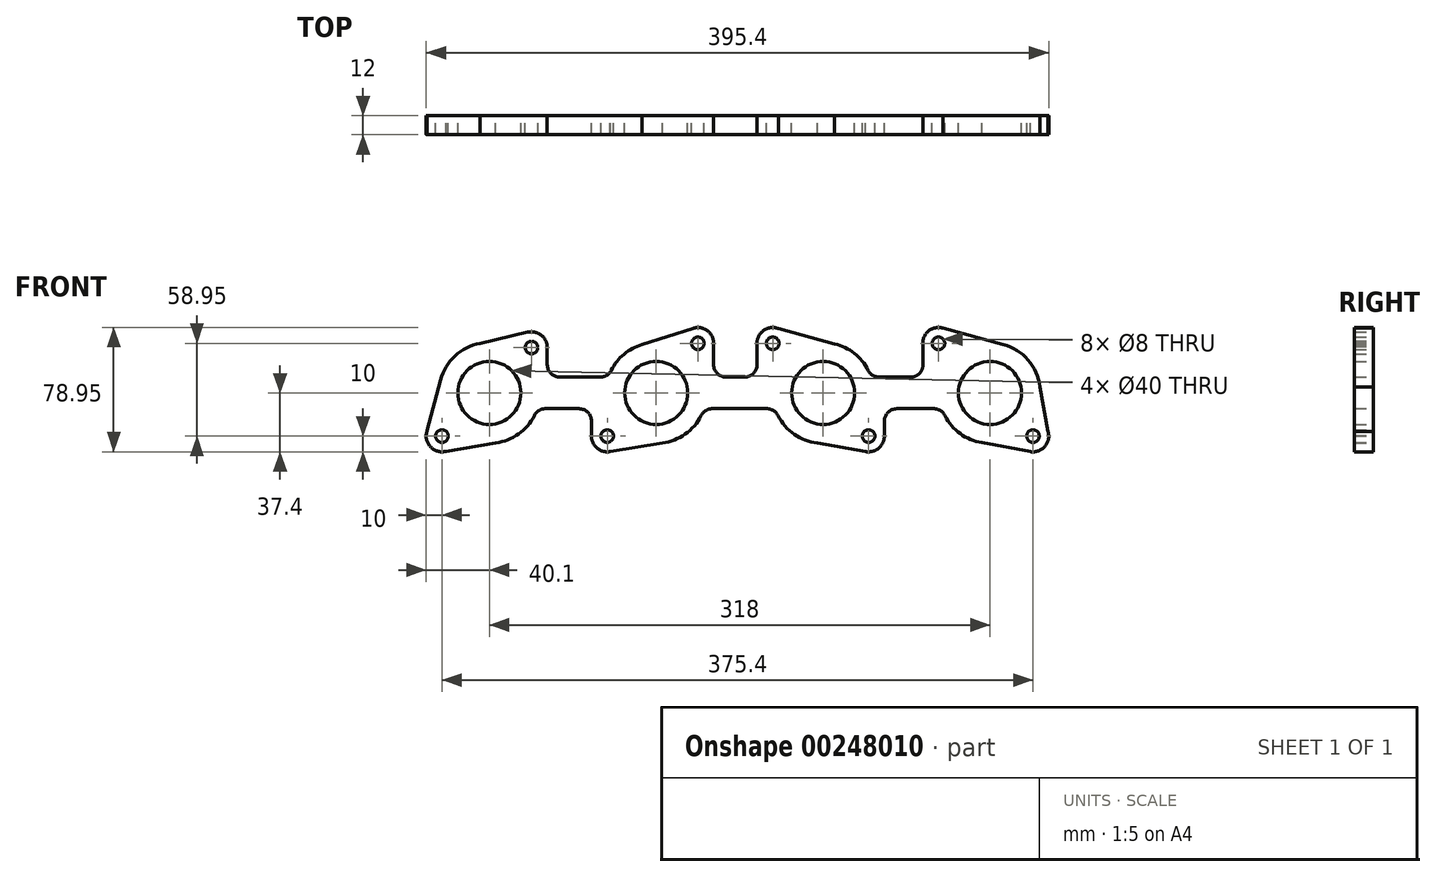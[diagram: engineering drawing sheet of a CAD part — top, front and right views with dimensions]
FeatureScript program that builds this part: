
annotation { "Feature Type Name" : "Feature", "Feature Type Description" : "" }
export const myFeature = defineFeature(function(context is Context, id is Id, definition is map)
    precondition{}
    {
        {
            var Q0;
            Q0=qCreatedBy(makeId("Front.planeOp"),FACE);
            var sketch = newSketch(context, id + "F0", { "sketchPlane" : qUnion([Q0])});
            skCircle(sketch, "E0", {"center": v(0, 0) * mm, "radius": 20 * mm});
            skCircle(sketch, "E1", {"center": v(106, 0) * mm, "radius": 20 * mm});
            skCircle(sketch, "E2", {"center": v(212, 0) * mm, "radius": 20 * mm});
            skCircle(sketch, "E3", {"center": v(26.8, 28.85) * mm, "radius": 4 * mm});
            skCircle(sketch, "E4", {"center": v(132.45, 31.55) * mm, "radius": 4 * mm});
            skCircle(sketch, "E5", {"center": v(180, 31.55) * mm, "radius": 4 * mm});
            skCircle(sketch, "E6", {"center": v(285.25, 31.55) * mm, "radius": 4 * mm});
            skCircle(sketch, "E7", {"center": v(-30.1, -27.4) * mm, "radius": 4 * mm});
            skCircle(sketch, "E8", {"center": v(74.9, -27.4) * mm, "radius": 4 * mm});
            skCircle(sketch, "E9", {"center": v(240.9, -27.4) * mm, "radius": 4 * mm});
            skCircle(sketch, "E10", {"center": v(345.3, -27.4) * mm, "radius": 4 * mm});
            skCircle(sketch, "E11", {"center": v(318, 0) * mm, "radius": 20 * mm});
            skArc(sketch, "E12", {"start": v(36.78, 28.3) * mm, "mid": v(33.2, 36.54) * mm, "end": v(24.43, 38.57) * mm});
            skArc(sketch, "E13", {"start": v(142.45, 31.49) * mm, "mid": v(138.37, 39.6) * mm, "end": v(129.4, 41.07) * mm});
            skArc(sketch, "E14", {"start": v(183.75, 40.82) * mm, "mid": v(174.24, 39.72) * mm, "end": v(170, 31.14) * mm});
            skArc(sketch, "E15", {"start": v(288.07, 41.14) * mm, "mid": v(279.2, 39.51) * mm, "end": v(275.25, 31.4) * mm});
            skArc(sketch, "E16", {"start": v(343.28, -37.2) * mm, "mid": v(352.72, -34.1) * mm, "end": v(354.84, -24.4) * mm});
            skArc(sketch, "E17", {"start": v(238.77, -37.17) * mm, "mid": v(247.26, -35.12) * mm, "end": v(250.9, -27.18) * mm});
            skArc(sketch, "E18", {"start": v(64.91, -26.93) * mm, "mid": v(68.36, -34.97) * mm, "end": v(76.8, -37.22) * mm});
            skArc(sketch, "E19", {"start": v(-39.46, -23.88) * mm, "mid": v(-37.48, -34.15) * mm, "end": v(-27.43, -37.04) * mm});
            skArc(sketch, "E20", {"start": v(240.58, 14.4) * mm, "mid": v(231.8, 25.14) * mm, "end": v(219.3, 31.16) * mm});
            skArc(sketch, "E21", {"start": v(289.42, -14.4) * mm, "mid": v(299.09, -25.81) * mm, "end": v(312.89, -31.59) * mm});
            skLineSegment(sketch, "E22", {"start": v(44.78, 10) * mm, "end": v(70.28, 10) * mm});
            skLineSegment(sketch, "E23", {"start": v(35.72, -10) * mm, "end": v(56.91, -10) * mm});
            skLineSegment(sketch, "E24.trimOffspring", {"start": v(150.45, 10) * mm, "end": v(162, 10) * mm});
            skLineSegment(sketch, "E25.trimOffspring", {"start": v(247.72, 10) * mm, "end": v(267.17, 10) * mm});
            skLineSegment(sketch, "E26.trimOffspring", {"start": v(258.9, -10) * mm, "end": v(282.28, -10) * mm});
            skArc(sketch, "E27.trimOffspring", {"start": v(183.42, -14.4) * mm, "mid": v(193.67, -26.23) * mm, "end": v(208.31, -31.79) * mm});
            skLineSegment(sketch, "E28.trimOffspring", {"start": v(141.72, -10) * mm, "end": v(176.28, -10) * mm});
            skArc(sketch, "E29.trimOffspring", {"start": v(109.88, -31.76) * mm, "mid": v(124.4, -26.18) * mm, "end": v(134.58, -14.4) * mm});
            skLineSegment(sketch, "E30", {"start": v(36.78, 29.4) * mm, "end": v(36.78, 18) * mm});
            skLineSegment(sketch, "E31", {"start": v(64.91, -26.93) * mm, "end": v(64.91, -18) * mm});
            skLineSegment(sketch, "E32", {"start": v(142.45, 31.61) * mm, "end": v(142.45, 18) * mm});
            skLineSegment(sketch, "E33", {"start": v(170, 31.96) * mm, "end": v(170, 18) * mm});
            skLineSegment(sketch, "E34", {"start": v(250.9, -27.18) * mm, "end": v(250.9, -18) * mm});
            skPoint(sketch, "E35.0.visualSharp", {"position": v(250.9, -10) * mm});
            skArc(sketch, "E35.0.filletArc", {"start": v(258.9, -10) * mm, "mid": v(253.24, -12.34) * mm, "end": v(250.9, -18) * mm});
            skPoint(sketch, "E36.0.newPointB", {"position": v(170, 10) * mm});
            skArc(sketch, "E36.0.filletArc", {"start": v(162, 10) * mm, "mid": v(167.67, 12.34) * mm, "end": v(170, 18) * mm});
            skPoint(sketch, "E37.0.newPointB", {"position": v(142.45, 10) * mm});
            skArc(sketch, "E37.0.filletArc", {"start": v(142.45, 18) * mm, "mid": v(144.8, 12.34) * mm, "end": v(150.45, 10) * mm});
            skArc(sketch, "E38.0.filletArc", {"start": v(64.91, -18) * mm, "mid": v(62.57, -12.34) * mm, "end": v(56.91, -10) * mm});
            skPoint(sketch, "E39.0.newPointA", {"position": v(36.78, 10) * mm});
            skArc(sketch, "E39.0.filletArc", {"start": v(36.78, 18) * mm, "mid": v(39.13, 12.34) * mm, "end": v(44.78, 10) * mm});
            skArc(sketch, "E40.trimOffspring", {"start": v(-5.87, 31.46) * mm, "mid": v(-21.76, 23.47) * mm, "end": v(-30.93, 8.22) * mm});
            skArc(sketch, "E41.trimOffspring", {"start": v(96.91, 30.68) * mm, "mid": v(85.48, 24.56) * mm, "end": v(77.42, 14.4) * mm});
            skLineSegment(sketch, "E42", {"start": v(219.3, 31.16) * mm, "end": v(183.75, 40.82) * mm});
            skLineSegment(sketch, "E43", {"start": v(238.77, -37.17) * mm, "end": v(208.31, -31.79) * mm});
            skLineSegment(sketch, "E44", {"start": v(96.91, 30.68) * mm, "end": v(129.4, 41.07) * mm});
            skLineSegment(sketch, "E45", {"start": v(109.88, -31.76) * mm, "end": v(76.8, -37.22) * mm});
            skPoint(sketch, "E45.endSnap0", {"position": v(76.8, -37.22) * mm});
            skLineSegment(sketch, "E46", {"start": v(76.8, -37.22) * mm, "end": v(76.8, -37.22) * mm});
            skPoint(sketch, "E47.0.visualSharp", {"position": v(75.6, 10) * mm});
            skArc(sketch, "E47.0.filletArc", {"start": v(70.28, 10) * mm, "mid": v(74.47, 11.19) * mm, "end": v(77.42, 14.4) * mm});
            skPoint(sketch, "E48.0.visualSharp", {"position": v(136.4, -10) * mm});
            skArc(sketch, "E48.0.filletArc", {"start": v(141.72, -10) * mm, "mid": v(137.53, -11.19) * mm, "end": v(134.58, -14.4) * mm});
            skPoint(sketch, "E49.0.visualSharp", {"position": v(181.6, -10) * mm});
            skArc(sketch, "E49.0.filletArc", {"start": v(183.42, -14.4) * mm, "mid": v(180.47, -11.19) * mm, "end": v(176.28, -10) * mm});
            skPoint(sketch, "E50.0.visualSharp", {"position": v(242.4, 10) * mm});
            skArc(sketch, "E50.0.filletArc", {"start": v(240.58, 14.4) * mm, "mid": v(243.53, 11.19) * mm, "end": v(247.72, 10) * mm});
            skPoint(sketch, "E51.0.visualSharp", {"position": v(287.6, -10) * mm});
            skArc(sketch, "E51.0.filletArc", {"start": v(289.42, -14.4) * mm, "mid": v(286.47, -11.19) * mm, "end": v(282.28, -10) * mm});
            skPoint(sketch, "E52.0.visualSharp", {"position": v(30.4, -10) * mm});
            skArc(sketch, "E52.0.filletArc", {"start": v(35.72, -10) * mm, "mid": v(31.53, -11.19) * mm, "end": v(28.58, -14.4) * mm});
            skLineSegment(sketch, "E53", {"start": v(24.43, 38.57) * mm, "end": v(-5.87, 31.46) * mm});
            skLineSegment(sketch, "E54", {"start": v(-39.46, -23.88) * mm, "end": v(-30.93, 8.22) * mm});
            skLineSegment(sketch, "E55", {"start": v(-27.43, -37.04) * mm, "end": v(4.09, -31.74) * mm});
            skArc(sketch, "E56.trimOffspring", {"start": v(4.09, -31.74) * mm, "mid": v(18.49, -26.12) * mm, "end": v(28.58, -14.4) * mm});
            skLineSegment(sketch, "E57", {"start": v(343.69, -37.27) * mm, "end": v(312.89, -31.59) * mm});
            skLineSegment(sketch, "E58", {"start": v(349.76, 3.88) * mm, "end": v(354.84, -24.4) * mm});
            skLineSegment(sketch, "E59", {"start": v(275.25, 31.4) * mm, "end": v(275.46, 18.12) * mm});
            skLineSegment(sketch, "E60", {"start": v(267.17, 10) * mm, "end": v(267.46, 10) * mm});
            skArc(sketch, "E61.0.filletArc", {"start": v(267.46, 10) * mm, "mid": v(273.16, 12.39) * mm, "end": v(275.46, 18.12) * mm});
            skLineSegment(sketch, "E62", {"start": v(288.07, 41.14) * mm, "end": v(326.28, 30.91) * mm});
            skArc(sketch, "E63.trimOffspring", {"start": v(349.76, 3.88) * mm, "mid": v(342.15, 20.99) * mm, "end": v(326.28, 30.91) * mm});
            skSolve(sketch);
        }
        {
            var Q0;
            Q0=makeQuery(id+"F0.imprint","IMPRINT",FACE,{"disambiguationData":[TD([[makeQuery(id+"F0.imprint","IMPRINT",EDGE,{"derivedFrom":sQuery(id+"F0.wireOp",EDGE,"E0")}),-1.0]])]});
            var Q1;
            {var subQ0=sQuery(id+"F0.wireOp",EDGE,"2MGUyzfr-QfrE-6VmW-v5Fb-fwrHkuR57WGK");Q1=makeQuery(id+"F0.imprint","IMPRINT",FACE,{"disambiguationData":[TD([[makeQuery(id+"F0.imprint","IMPRINT",EDGE,{"derivedFrom":subQ0}),1.0]])]});}
            var Q2;
            {var subQ0=sQuery(id+"F0.wireOp",EDGE,"jCVJHCwx-2gE8-7g3H-6rGu-MTP52CmHTdXj");Q2=makeQuery(id+"F0.imprint","IMPRINT",FACE,{"disambiguationData":[TD([[makeQuery(id+"F0.imprint","IMPRINT",EDGE,{"derivedFrom":subQ0}),1.0]])]});}
            var Q3;
            {var subQ0=sQuery(id+"F0.wireOp",EDGE,"d8a2bccd-10a2-4388-9793-c8e3900107fc.trimOffspring");Q3=makeQuery(id+"F0.imprint","IMPRINT",FACE,{"disambiguationData":[TD([[makeQuery(id+"F0.imprint","IMPRINT",EDGE,{"derivedFrom":subQ0}),1.0]])]});}
            var Q4;
            {var subQ4=sQuery(id+"F0.wireOp",EDGE,"1AFlqpd6-JihM-TW57-sDu2-bnsLzhxU2nBO");Q4=makeQuery(id+"F0.imprint","IMPRINT",FACE,{"disambiguationData":[TD([[makeQuery(id+"F0.imprint","IMPRINT",EDGE,{"derivedFrom":subQ4}),1.0]])]});}
            var Q5;
            {var subQ0=sQuery(id+"F0.wireOp",EDGE,"ffIl8IeB-IDaS-1Qld-qKGN-nhHRXU7NPppc");Q5=makeQuery(id+"F0.imprint","IMPRINT",FACE,{"disambiguationData":[TD([[makeQuery(id+"F0.imprint","IMPRINT",EDGE,{"derivedFrom":subQ0}),1.0]])]});}
            var Q6;
            {var subQ0=sQuery(id+"F0.wireOp",EDGE,"BHNejNgT-LVu3-s0kJ-r63Y-hWjsq5vZP9YP");var subQ6=sQuery(id+"F0.wireOp",EDGE,"uM61tjMx-ujBO-MmZV-Et5Y-2aCRGrYZROLU");var subQ10=makeQuery(id+"F0.imprint","INTERSECT",VERTEX,{"derivedFrom":[subQ6,subQ0]});Q6=makeQuery(id+"F0.imprint","IMPRINT",FACE,{"disambiguationData":[TD([[makeQuery(id+"F0.imprint","IMPRINT",EDGE,{"disambiguationData":[TD([[subQ10,-1.0]])],"derivedFrom":subQ6}),1.0]])]});}
            var Q7;
            {var subQ0=sQuery(id+"F0.wireOp",EDGE,"4uetbdvp-1b4e-eopa-coM4-gb9XXig9Qzif");Q7=makeQuery(id+"F0.imprint","IMPRINT",FACE,{"disambiguationData":[TD([[makeQuery(id+"F0.imprint","IMPRINT",EDGE,{"derivedFrom":subQ0}),1.0]])]});}
            var Q8;
            {var subQ0=sQuery(id+"F0.wireOp",EDGE,"8008c4f2-338b-4719-8728-eb8934cf37c9.trimOffspring");Q8=makeQuery(id+"F0.imprint","IMPRINT",FACE,{"disambiguationData":[TD([[makeQuery(id+"F0.imprint","IMPRINT",EDGE,{"derivedFrom":subQ0}),1.0]])]});}
            var Q9;
            {var subQ1=sQuery(id+"F0.wireOp",EDGE,"uM61tjMx-ujBO-MmZV-Et5Y-2aCRGrYZROLU");var subQ3=sQuery(id+"F0.wireOp",EDGE,"Of9Iz9Od-6Ep9-KKgw-OSyH-3CGtNpXtkhQ5");var subQ9=makeQuery(id+"F0.imprint","INTERSECT",VERTEX,{"derivedFrom":[subQ1,subQ3]});Q9=makeQuery(id+"F0.imprint","IMPRINT",FACE,{"disambiguationData":[TD([[makeQuery(id+"F0.imprint","IMPRINT",EDGE,{"disambiguationData":[TD([[subQ9,-1.0]])],"derivedFrom":subQ1}),1.0]])]});}
            var Q10;
            {var subQ0=sQuery(id+"F0.wireOp",EDGE,"lNeG5BkU-q91e-Xypx-oDSb-jSm0idHaWxNC");Q10=makeQuery(id+"F0.imprint","IMPRINT",FACE,{"disambiguationData":[TD([[makeQuery(id+"F0.imprint","IMPRINT",EDGE,{"derivedFrom":subQ0}),1.0]])]});}
            var Q11;
            {var subQ0=sQuery(id+"F0.wireOp",EDGE,"c371198c-ccad-4cd7-b4d3-06cf283aa17a.trimOffspring");Q11=makeQuery(id+"F0.imprint","IMPRINT",FACE,{"disambiguationData":[TD([[makeQuery(id+"F0.imprint","IMPRINT",EDGE,{"derivedFrom":subQ0}),1.0]])]});}
            extrude(context, id + "F1", {"entities" : qUnion([Q0, Q1, Q2, Q3, Q4, Q5, Q6, Q7, Q8, Q9, Q10, Q11]), "depth" : 12 * mm});
        }
    });
